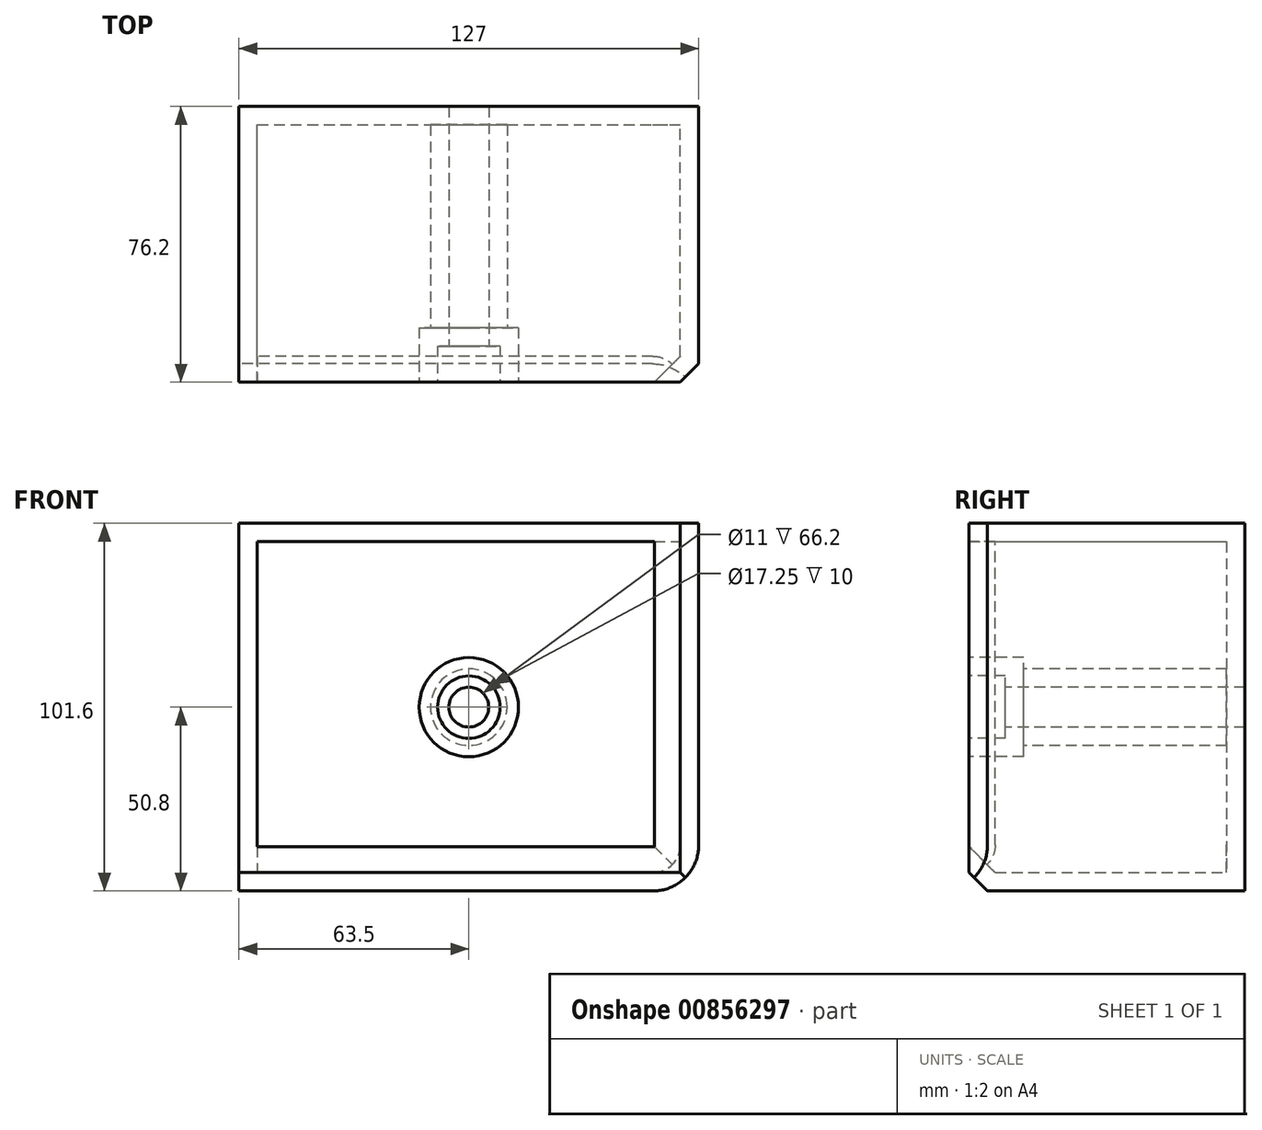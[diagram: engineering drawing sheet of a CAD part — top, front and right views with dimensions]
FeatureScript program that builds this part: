
annotation { "Feature Type Name" : "Feature", "Feature Type Description" : "" }
export const myFeature = defineFeature(function(context is Context, id is Id, definition is map)
    precondition{}
    {
        {
            var Q0;
            Q0=qCreatedBy(makeId("Front.planeOp"),FACE);
            var sketch = newSketch(context, id + "F0", { "sketchPlane" : qUnion([Q0])});
            skLineSegment(sketch, "E0.bottom", {"start": v(-25.4, 25.4) * mm, "end": v(101.6, 25.4) * mm});
            skLineSegment(sketch, "E0.top", {"start": v(-25.4, -76.2) * mm, "end": v(101.6, -76.2) * mm});
            skLineSegment(sketch, "E0.left", {"start": v(-25.4, 25.4) * mm, "end": v(-25.4, -76.2) * mm});
            skLineSegment(sketch, "E0.right", {"start": v(101.6, 25.4) * mm, "end": v(101.6, -76.2) * mm});
            skSolve(sketch);
        }
        {
            var Q0;
            Q0=makeQuery(id+"F0.imprint","IMPRINT",FACE,{"disambiguationData":[TD([[makeQuery(id+"F0.imprint","IMPRINT",EDGE,{"derivedFrom":sQuery(id+"F0.wireOp",EDGE,"E0.bottom")}),-1.0]])]});
            extrude(context, id + "F1", {"entities" : qUnion([Q0]), "depth" : 76.2 * mm, "offsetDistance" : 25.4 * mm});
        }
        {
            var Q0;
            Q0=makeQuery(id+"F1.opExtrude","CAP_FACE",FACE,{"disambiguationData":[OSD([sQuery(id+"F0.wireOp",EDGE,"E0.bottom"),sQuery(id+"F0.wireOp",EDGE,"E0.top"),sQuery(id+"F0.wireOp",EDGE,"E0.left"),sQuery(id+"F0.wireOp",EDGE,"E0.right")])],"isStart":false});
            var sketch = newSketch(context, id + "F2", { "sketchPlane" : qUnion([Q0])});
            skPoint(sketch, "E1", {"position": v(38.1, -25.4) * mm});
            skSolve(sketch);
        }
        {
            var Q0;
            Q0=sQuery(id+"F2.wireOp",VERTEX,"E1");
            var Q1;
            Q1=makeQuery(id+"F1.opExtrude","SWEPT_BODY",BODY,{"disambiguationData":[OSD([sQuery(id+"F0.wireOp",EDGE,"E0.bottom"),sQuery(id+"F0.wireOp",EDGE,"E0.top"),sQuery(id+"F0.wireOp",EDGE,"E0.left"),sQuery(id+"F0.wireOp",EDGE,"E0.right")])]});
            hole(context, id + "F3", {"style" : HoleStyle.C_BORE, "endStyle" : HoleEndStyle.THROUGH, "standardTappedOrClearance" : lookupTablePath({ "fit" : "Normal", "standard" : "ISO", "size" : "M10", "type" : "Clearance" }), "standardBlindInLast" : lookupTablePath({ "fit" : "Standard", "standard" : "ISO", "size" : "M10", "type" : "Clearance" }), "holeDiameter" : 11 * mm, "cBoreDiameter" : 17.25 * mm, "cBoreDepth" : 10 * mm, "majorDiameter" : 6.35 * mm, "isTappedThrough" : true, "tappedDepth" : 12.7 * mm, "tapClearance" : 3, "locations" : qUnion([Q0]), "scope" : qUnion([Q1])});
        }
        {
            var Q0;
            Q0=makeQuery(id+"F1.opExtrude","CAP_EDGE",EDGE,{"disambiguationData":[OSD([sQuery(id+"F0.wireOp",EDGE,"E0.top")])],"isStart":false});
            var Q1;
            Q1=makeQuery(id+"F1.opExtrude","CAP_EDGE",EDGE,{"disambiguationData":[OSD([sQuery(id+"F0.wireOp",EDGE,"E0.right")])],"isStart":false});
            chamfer(context, id + "F4", {"entities" : qUnion([Q0, Q1]), "width" : 5.08 * mm, "tangentPropagation" : true});
        }
        {
            var Q0;
            Q0=makeQuery(id+"F1.opExtrude","SWEPT_EDGE",EDGE,{"disambiguationData":[OSD([sQuery(id+"F0.wireOp",EDGE,"E0.top"),sQuery(id+"F0.wireOp",EDGE,"E0.right")])]});
            fillet(context, id + "F5", {"entities" : qUnion([Q0]), "radius" : 12.7 * mm, "tangentPropagation" : true, "allowEdgeOverflow" : false});
        }
        {
            var Q0;
            Q0=makeQuery(id+"F1.opExtrude","CAP_FACE",FACE,{"disambiguationData":[OSD([sQuery(id+"F0.wireOp",EDGE,"E0.bottom"),sQuery(id+"F0.wireOp",EDGE,"E0.top"),sQuery(id+"F0.wireOp",EDGE,"E0.left"),sQuery(id+"F0.wireOp",EDGE,"E0.right")])],"isStart":false});
            shell(context, id + "F6", {"entities" : qUnion([Q0]), "thickness" : 5.08 * mm});
        }
    });
